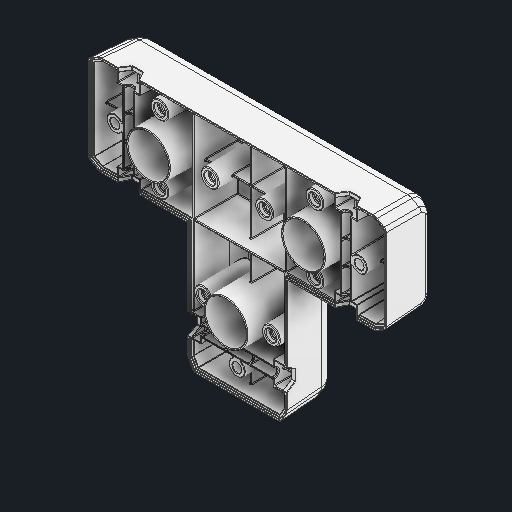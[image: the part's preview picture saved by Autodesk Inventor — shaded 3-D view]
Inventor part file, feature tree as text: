
AUTODESK INVENTOR PART (.ipt)
format: ipt  version: 2025 (Build 290162000, 162)  size: 4,939,264 bytes
history: native  units: in
note: dims shown in document units (in); Inventor stores cm internally (conversion verified against a paired STEP export)
features: fillet x1
ambient origin geometry x8: Origin, YZ Plane, XZ Plane, XY Plane, X Axis, Y Axis, Z Axis, Center Point
bodies: Solid1 (feature_tree)
feature tree (1):
  fillet  "Fillet31"  [1 undecoded]
note: 1 required parameter value undecoded (feature->parameter linkage not recoverable at this tier; creation-order binding heuristic only, values carry confidence <= 0.55)
